# Revit family: QF_BOURGEAT_chariots_plein
name_source: partatom
category: Equipement spécialisé
revit_build: Autodesk Revit 2015 (Build: 20140606_1530(x64)
units: mm (PartAtom-declared; Revit-internal decimal feet)

## types (3) — shared parameters
Charge max = 160.00 kg
Fabricant = BOURGEAT
Hauteur hors tout = 900 mm  [stored 2.95276 ft]
Longueur hors tout = 990 mm  [stored 3.24803 ft]
Poids net à vide = 55.00 kg
Profondeur hors tout = 510 mm  [stored 1.67323 ft]
URL catalogue = http://www.bourgeat.fr
larg_corps = 890 mm  [stored 2.91995 ft]
prof_corps = 466 mm  [stored 1.52887 ft]

## per-type parameters (varying)
| type | Fréquence | Indice de protection | Intensité nominale | Modèle | Phase | Puissance électrique  | Spécification du Fabricant | Tension |
| chauffant_non_ventile_assiettes_120/180 | 50 Hz | 21 | 6 A | 777604 + 777641 | 2 | 1400 W | CHARIOTS UNIVERSELS | 230 V |
| chauffant_ventile_assiettes_120/180 | 50 Hz | 21 | 6 A | 777606 + 777641 | 2 | 1400 W | CHARIOTS UNIVERSELS | 230 V |
| neutre_assiettes120/180 | 0 Hz |  | 0 A | 777516 + 777641 | 0 | 0 W | CHARIOT UNIVERSEL | 0 V |

note: [stored X ft] marks values corroborated as IEEE doubles in the binary element streams (Revit-internal decimal feet)
